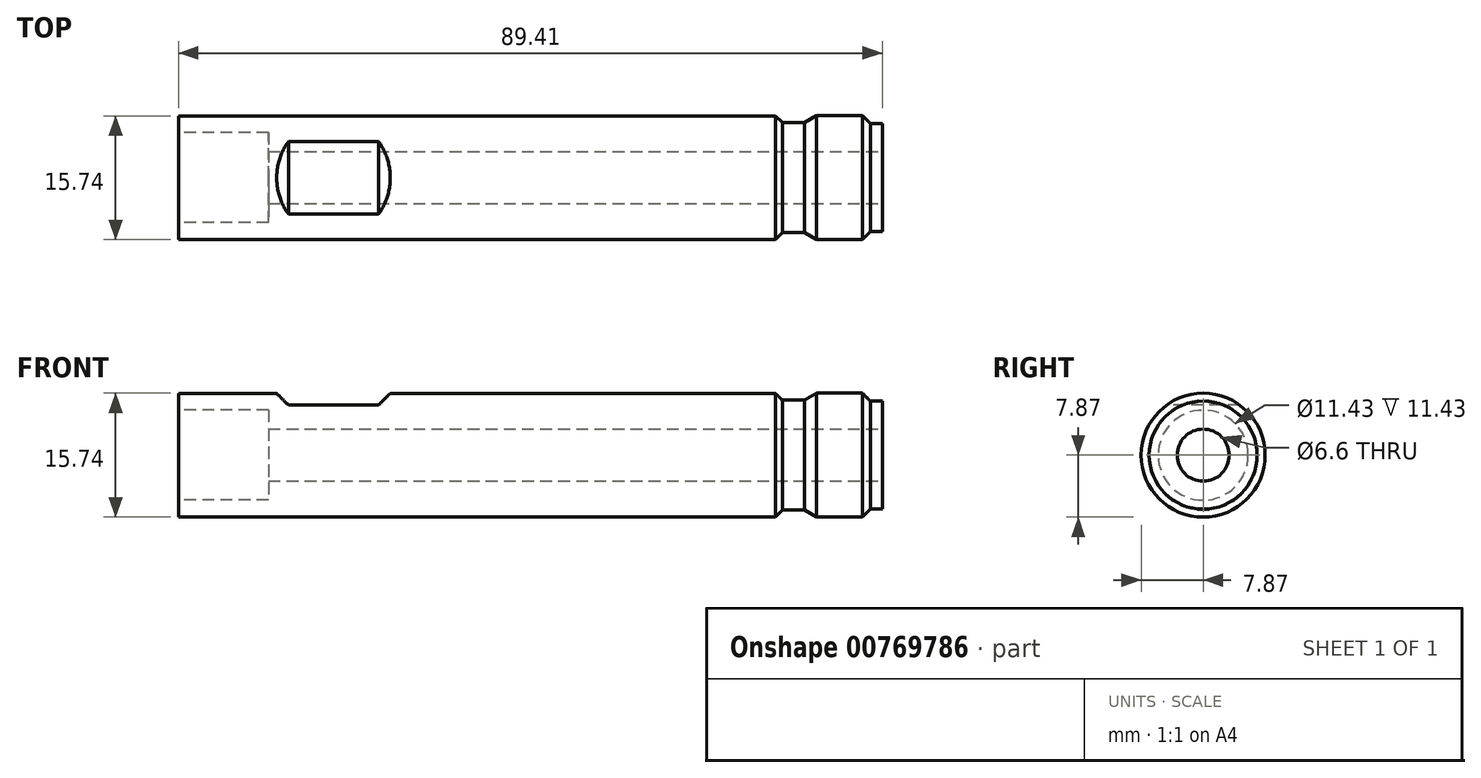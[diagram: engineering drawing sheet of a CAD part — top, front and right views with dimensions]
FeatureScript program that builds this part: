
annotation { "Feature Type Name" : "Feature", "Feature Type Description" : "" }
export const myFeature = defineFeature(function(context is Context, id is Id, definition is map)
    precondition{}
    {
        {
            var Q0;
            Q0=qCreatedBy(makeId("Front.planeOp"),FACE);
            var sketch = newSketch(context, id + "F0", { "sketchPlane" : qUnion([Q0])});
            skLineSegment(sketch, "E0", {"start": v(0, 0) * mm, "end": v(145.57, 0) * mm, "construction": true});
            skLineSegment(sketch, "E1", {"start": v(0, 7.85) * mm, "end": v(75.84, 7.85) * mm});
            skLineSegment(sketch, "E2", {"start": v(75.84, 7.85) * mm, "end": v(76.7, 6.98) * mm});
            skLineSegment(sketch, "E3", {"start": v(76.7, 6.99) * mm, "end": v(79.5, 6.99) * mm});
            skLineSegment(sketch, "E4", {"start": v(79.5, 6.99) * mm, "end": v(81.04, 7.87) * mm});
            skLineSegment(sketch, "E5", {"start": v(81.04, 7.87) * mm, "end": v(86.87, 7.87) * mm});
            skLineSegment(sketch, "E6", {"start": v(86.87, 7.87) * mm, "end": v(87.88, 6.86) * mm});
            skLineSegment(sketch, "E7", {"start": v(87.88, 6.86) * mm, "end": v(89.4, 6.86) * mm});
            skLineSegment(sketch, "E8", {"start": v(89.4, 6.86) * mm, "end": v(89.4, 0) * mm});
            skLineSegment(sketch, "E9", {"start": v(89.4, 0) * mm, "end": v(11.43, 0) * mm});
            skLineSegment(sketch, "E10", {"start": v(11.43, 0) * mm, "end": v(11.43, 5.72) * mm});
            skLineSegment(sketch, "E11", {"start": v(11.43, 5.72) * mm, "end": v(0, 5.71) * mm});
            skLineSegment(sketch, "E12", {"start": v(0, 5.72) * mm, "end": v(0, 7.85) * mm});
            skSolve(sketch);
        }
        {
            var Q0;
            Q0=makeQuery(id+"F0.imprint","IMPRINT",FACE,{"disambiguationData":[TD([[makeQuery(id+"F0.imprint","IMPRINT",EDGE,{"derivedFrom":sQuery(id+"F0.wireOp",EDGE,"E1")}),-1.0]])]});
            var Q1;
            Q1=sQuery(id+"F0.wireOp",EDGE,"E0");
            revolve(context, id + "F1", {"surfaceOperationType" : NewSurfaceOperationType.NEW, "entities" : qUnion([Q0]), "axis" : qUnion([Q1]), "revolveType" : RevolveType.FULL});
        }
        {
            var Q0;
            Q0=makeQuery(id+"F1.opRevolve","SWEPT_FACE",FACE,{"disambiguationData":[OSD([sQuery(id+"F0.wireOp",EDGE,"E8")])]});
            var sketch = newSketch(context, id + "F2", { "sketchPlane" : qUnion([Q0])});
            skCircle(sketch, "E13", {"center": v(0, 0) * mm, "radius": 3.3 * mm});
            skSolve(sketch);
        }
        {
            var Q0;
            Q0=makeQuery(id+"F2.imprint","IMPRINT",FACE,{"disambiguationData":[TD([[makeQuery(id+"F2.imprint","IMPRINT",EDGE,{"derivedFrom":sQuery(id+"F2.wireOp",EDGE,"E13")}),1.0]])]});
            extrude(context, id + "F3", {"entities" : qUnion([Q0]), "operationType" : NewBodyOperationType.REMOVE, "endBound" : BoundingType.THROUGH_ALL, "oppositeDirection" : true, "depth" : 25.4 * mm, "offsetDistance" : 25.4 * mm});
        }
        {
            var Q0;
            Q0=qCreatedBy(makeId("Front.planeOp"),FACE);
            var sketch = newSketch(context, id + "F4", { "sketchPlane" : qUnion([Q0])});
            skLineSegment(sketch, "E14", {"start": v(13.97, 6.35) * mm, "end": v(25.4, 6.35) * mm});
            skLineSegment(sketch, "E15", {"start": v(13.97, 6.35) * mm, "end": v(0, 20.32) * mm});
            skLineSegment(sketch, "E16", {"start": v(0, 20.32) * mm, "end": v(39.37, 20.32) * mm});
            skLineSegment(sketch, "E17", {"start": v(39.37, 20.32) * mm, "end": v(25.4, 6.35) * mm});
            skSolve(sketch);
        }
        {
            var Q0;
            Q0=makeQuery(id+"F4.imprint","IMPRINT",FACE,{"disambiguationData":[TD([[makeQuery(id+"F4.imprint","IMPRINT",EDGE,{"derivedFrom":sQuery(id+"F4.wireOp",EDGE,"E14")}),1.0]])]});
            extrude(context, id + "F5", {"entities" : qUnion([Q0]), "operationType" : NewBodyOperationType.REMOVE, "endBound" : BoundingType.SYMMETRIC, "oppositeDirection" : true, "depth" : 25.4 * mm, "offsetDistance" : 25.4 * mm});
        }
    });
